# Revit family: WAGNER_Тройник_для_скрытого_монтажа_PVC
name_source: partatom
category: Арматура трубопроводов
units: mm (PartAtom-declared; Revit-internal decimal feet)

## family parameters
Всегда вертикально = Да
Заголовок OmniClass = Pipework Fittings
На основе рабочей плоскости = Нет
Номер OmniClass = 23.60.30.11.14
Общий = Да
При загрузке вырезать с полостями = Нет
Размер круглого соединителя = Использовать диаметр
Тип детали = Нормальный

## types (1)
- Typ R-RH
    ADSK_URL документации изделия = https://ru.wagnergroup.com
    ADSK_URL страницы изделия = https://ru.wagnergroup.com
    ADSK_Версия Revit = Revit 2017
    ADSK_Версия семейства = Версия 1
    ADSK_Дата изменения = 19.07.20
    ADSK_Единица измерения = шт.
    ADSK_Завод-изготовитель = WAGNER
    ADSK_Код изделия = -
    ADSK_Марка = Typ R-RH
    ADSK_Материал = WAGNER_PVC
    ADSK_Наименование = Тройник для скрытого монтажа
    ADSK_Наименование краткое = Тройник
    ADSK_Размер_Высота = 0 мм
    ADSK_Размер_Длина = 0 мм
    ADSK_Размер_Ширина = 0 мм
    COBie Category = Pipework Fittings
    Masterformat Code = 22 01 10
    Masterformat Title = Pipe and pumps
    OmniClass Code = 23-27 43 15
    OmniClass Title = Pipe Expansion Joints
    UNSPSC Code = 40142319
    UNSPSC Title = Pipe tees
    URL = www.wagner-russia.com
    Uniclass Code = Ac_10_40_63
    Uniclass Title = Pipe fitting
    WAGNER_Variation = 1
    WAGNER_Артикул = 01-10-9300
    WAGNER_Название = Тройник для скрытого монтажа PVC
    WAGNER_Температурный режим. = от -20℃ до +60℃
    WAGNER_Тип = Typ R-RH
    bimon.ru = bimon.ru
    Изготовитель = WAGNER
    Описание = Тройник для скрытого монтажа
    Отметка по умолчанию = 0 мм
